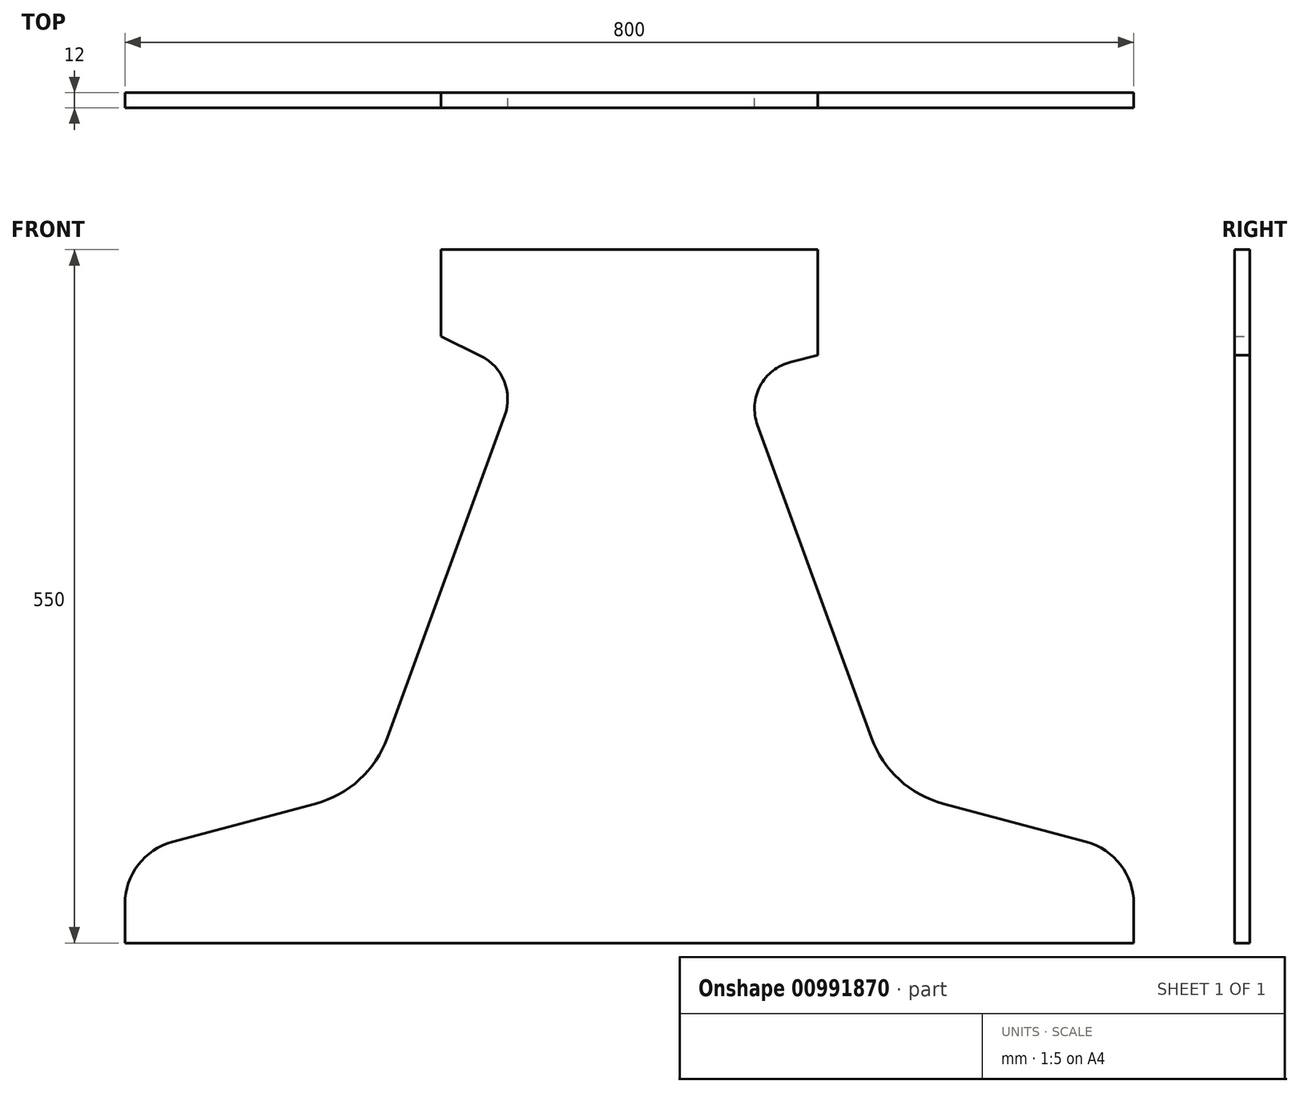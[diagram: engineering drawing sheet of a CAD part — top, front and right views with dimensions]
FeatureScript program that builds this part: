
annotation { "Feature Type Name" : "Feature", "Feature Type Description" : "" }
export const myFeature = defineFeature(function(context is Context, id is Id, definition is map)
    precondition{}
    {
        {
            var Q0;
            Q0=qCreatedBy(makeId("Front.planeOp"),FACE);
            var sketch = newSketch(context, id + "F0", { "sketchPlane" : qUnion([Q0])});
            skLineSegment(sketch, "E0.top", {"start": v(-385.24, -247.77) * mm, "end": v(414.76, -247.77) * mm});
            skLineSegment(sketch, "E0.left", {"start": v(-385.24, -216.75) * mm, "end": v(-385.24, -247.77) * mm});
            skLineSegment(sketch, "E0.right", {"start": v(414.76, -216.75) * mm, "end": v(414.76, -247.77) * mm});
            skLineSegment(sketch, "E1", {"start": v(-347.59, -167.68) * mm, "end": v(-234.2, -137.3) * mm});
            skLineSegment(sketch, "E2", {"start": v(263.72, -137.3) * mm, "end": v(377.1, -167.68) * mm});
            skLineSegment(sketch, "E3", {"start": v(-177.13, -85) * mm, "end": v(-84.06, 170.7) * mm});
            skLineSegment(sketch, "E4", {"start": v(-134.77, 233.47) * mm, "end": v(-134.77, 302.23) * mm});
            skLineSegment(sketch, "E5", {"start": v(-134.77, 302.23) * mm, "end": v(164.29, 302.23) * mm});
            skLineSegment(sketch, "E6", {"start": v(164.29, 302.23) * mm, "end": v(164.29, 218.5) * mm});
            skLineSegment(sketch, "E7", {"start": v(116.33, 163.15) * mm, "end": v(206.65, -85) * mm});
            skLineSegment(sketch, "E8", {"start": v(142.89, 213.15) * mm, "end": v(164.29, 218.5) * mm});
            skLineSegment(sketch, "E9", {"start": v(-103.1, 217.95) * mm, "end": v(-134.77, 233.47) * mm});
            skPoint(sketch, "E10.visualSharp", {"position": v(221.58, -126) * mm});
            skArc(sketch, "E10.filletArc", {"start": v(206.65, -85) * mm, "mid": v(228.79, -118.13) * mm, "end": v(263.72, -137.3) * mm});
            skPoint(sketch, "E11.visualSharp", {"position": v(414.76, -177.77) * mm});
            skArc(sketch, "E11.filletArc", {"start": v(414.76, -216.75) * mm, "mid": v(404.26, -185.82) * mm, "end": v(377.1, -167.68) * mm});
            skPoint(sketch, "E12.visualSharp", {"position": v(101.87, 202.89) * mm});
            skArc(sketch, "E12.filletArc", {"start": v(142.89, 213.15) * mm, "mid": v(118.49, 194.06) * mm, "end": v(116.33, 163.15) * mm});
            skPoint(sketch, "E13.visualSharp", {"position": v(-72.35, 202.89) * mm});
            skArc(sketch, "E13.filletArc", {"start": v(-84.06, 170.7) * mm, "mid": v(-84.52, 197.98) * mm, "end": v(-103.1, 217.95) * mm});
            skPoint(sketch, "E14.visualSharp", {"position": v(-192.05, -126) * mm});
            skArc(sketch, "E14.filletArc", {"start": v(-234.2, -137.3) * mm, "mid": v(-199.27, -118.13) * mm, "end": v(-177.13, -85) * mm});
            skPoint(sketch, "E15.visualSharp", {"position": v(-385.24, -177.77) * mm});
            skArc(sketch, "E15.filletArc", {"start": v(-347.59, -167.68) * mm, "mid": v(-374.74, -185.82) * mm, "end": v(-385.24, -216.75) * mm});
            skSolve(sketch);
        }
        {
            var Q0;
            Q0=qSketchRegion(id+"F0",true);
            extrude(context, id + "F1", {"entities" : qUnion([Q0]), "depth" : 12 * mm, "offsetDistance" : 25.4 * mm});
        }
    });
